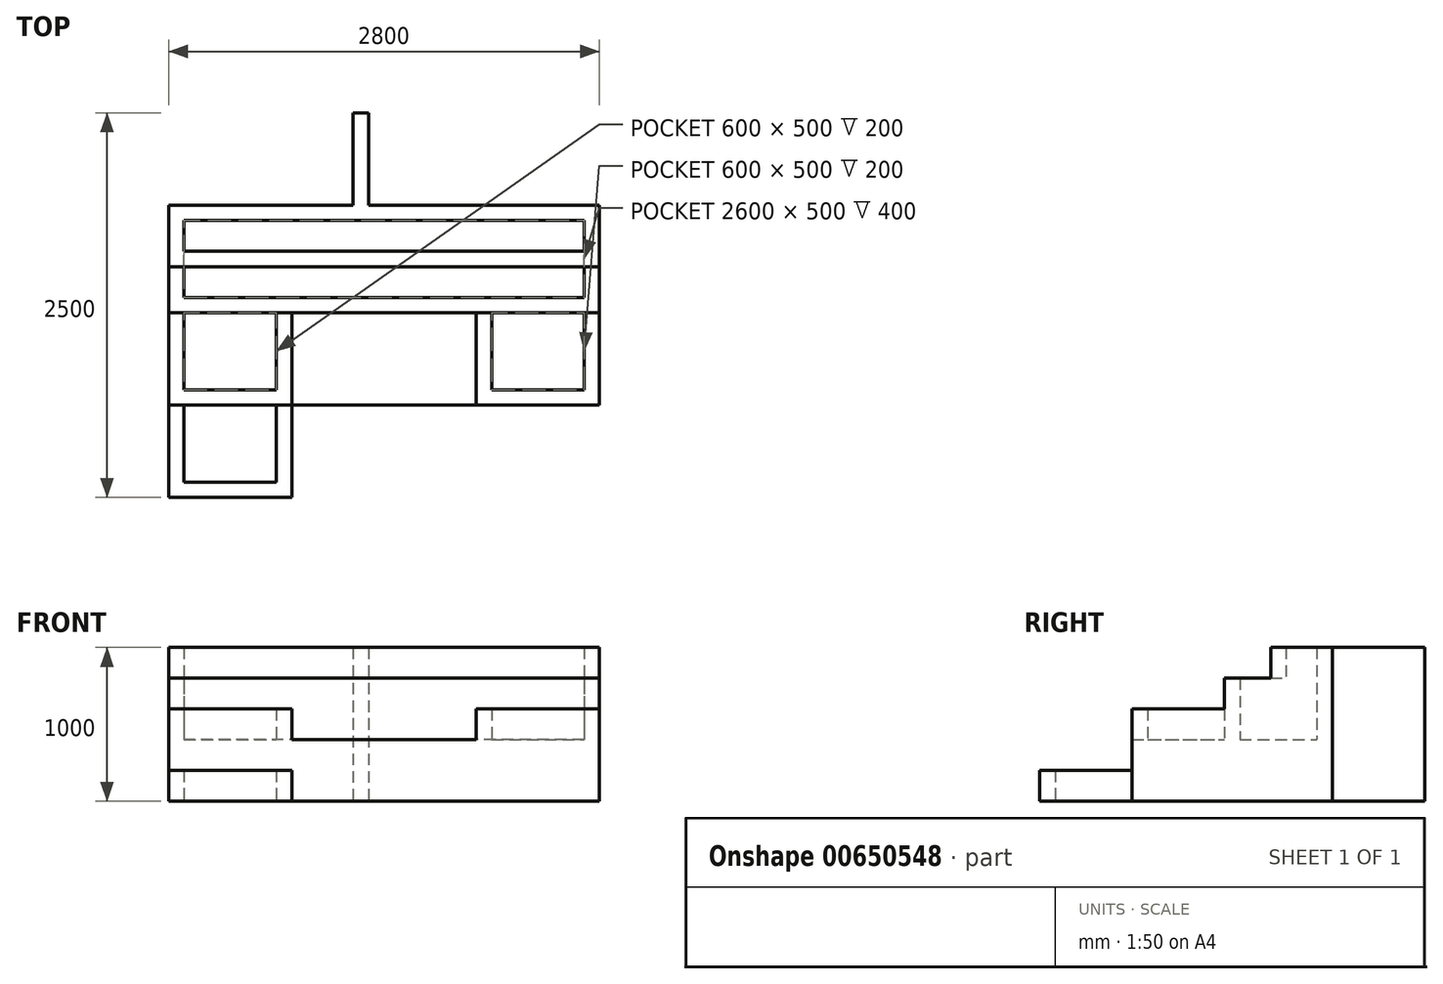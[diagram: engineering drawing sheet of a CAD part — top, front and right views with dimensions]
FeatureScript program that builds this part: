
annotation { "Feature Type Name" : "Feature", "Feature Type Description" : "" }
export const myFeature = defineFeature(function(context is Context, id is Id, definition is map)
    precondition{}
    {
        {
            var Q0;
            Q0=qCreatedBy(makeId("Top.planeOp"),FACE);
            var sketch = newSketch(context, id + "F0", { "sketchPlane" : qUnion([Q0])});
            skLineSegment(sketch, "E0.bottom", {"start": v(0, 0) * mm, "end": v(-2800, 0) * mm});
            skLineSegment(sketch, "E0.top", {"start": v(0, 1300) * mm, "end": v(-2800, 1300) * mm});
            skLineSegment(sketch, "E0.left", {"start": v(0, 0) * mm, "end": v(0, 1300) * mm});
            skLineSegment(sketch, "E0.right", {"start": v(-2800, 0) * mm, "end": v(-2800, 1300) * mm});
            skSolve(sketch);
        }
        {
            var Q0;
            Q0=makeQuery(id+"F0.imprint","IMPRINT",FACE,{"disambiguationData":[TD([[makeQuery(id+"F0.imprint","IMPRINT",EDGE,{"derivedFrom":sQuery(id+"F0.wireOp",EDGE,"E0.bottom")}),-1.0]])]});
            extrude(context, id + "F1", {"entities" : qUnion([Q0]), "depth" : 400 * mm, "offsetDistance" : 25 * mm});
        }
        {
            var Q0;
            Q0=makeQuery(id+"F1.opExtrude","CAP_FACE",FACE,{"disambiguationData":[OSD([sQuery(id+"F0.wireOp",EDGE,"E0.bottom"),sQuery(id+"F0.wireOp",EDGE,"E0.top"),sQuery(id+"F0.wireOp",EDGE,"E0.left"),sQuery(id+"F0.wireOp",EDGE,"E0.right"),sQuery(id+"F0.wireOp",EDGE,"GwEAKkGj-kL16-nnvY-5oqN-CwZshuGkm8Sl.bottom"),sQuery(id+"F0.wireOp",EDGE,"GwEAKkGj-kL16-nnvY-5oqN-CwZshuGkm8Sl.top"),sQuery(id+"F0.wireOp",EDGE,"GwEAKkGj-kL16-nnvY-5oqN-CwZshuGkm8Sl.left"),sQuery(id+"F0.wireOp",EDGE,"GwEAKkGj-kL16-nnvY-5oqN-CwZshuGkm8Sl.right")])],"isStart":false});
            var sketch = newSketch(context, id + "F2", { "sketchPlane" : qUnion([Q0])});
            skLineSegment(sketch, "E1.bottom", {"start": v(0, 600) * mm, "end": v(-2800, 600) * mm});
            skLineSegment(sketch, "E1.top", {"start": v(0, 1300) * mm, "end": v(-2800, 1300) * mm});
            skLineSegment(sketch, "E1.left", {"start": v(0, 600) * mm, "end": v(0, 1300) * mm});
            skLineSegment(sketch, "E1.right", {"start": v(-2800, 600) * mm, "end": v(-2800, 1300) * mm});
            skLineSegment(sketch, "E2.bottom", {"start": v(-100, 700) * mm, "end": v(-2700, 700) * mm});
            skLineSegment(sketch, "E2.top", {"start": v(-100, 1200) * mm, "end": v(-2700, 1200) * mm});
            skLineSegment(sketch, "E2.left", {"start": v(-100, 700) * mm, "end": v(-100, 1200) * mm});
            skLineSegment(sketch, "E2.right", {"start": v(-2700, 700) * mm, "end": v(-2700, 1200) * mm});
            skSolve(sketch);
        }
        {
            var Q0;
            Q0=qSketchRegion(id+"F2",true);
            extrude(context, id + "F3", {"entities" : qUnion([Q0]), "operationType" : NewBodyOperationType.ADD, "depth" : 400 * mm, "offsetDistance" : 25 * mm});
        }
        {
            var Q0;
            Q0=makeQuery(id+"F3.opExtrude","CAP_FACE",FACE,{"disambiguationData":[OSD([sQuery(id+"F2.wireOp",EDGE,"E1.bottom"),sQuery(id+"F2.wireOp",EDGE,"E1.top"),sQuery(id+"F2.wireOp",EDGE,"E1.left"),sQuery(id+"F2.wireOp",EDGE,"E1.right"),sQuery(id+"F2.wireOp",EDGE,"E2.bottom"),sQuery(id+"F2.wireOp",EDGE,"E2.top"),sQuery(id+"F2.wireOp",EDGE,"E2.left"),sQuery(id+"F2.wireOp",EDGE,"E2.right")])],"isStart":false});
            var sketch = newSketch(context, id + "F4", { "sketchPlane" : qUnion([Q0])});
            skLineSegment(sketch, "E3.bottom", {"start": v(0, 900) * mm, "end": v(-2800, 900) * mm});
            skLineSegment(sketch, "E3.top", {"start": v(0, 1300) * mm, "end": v(-2800, 1300) * mm});
            skLineSegment(sketch, "E3.left", {"start": v(0, 900) * mm, "end": v(0, 1300) * mm});
            skLineSegment(sketch, "E3.right", {"start": v(-2800, 900) * mm, "end": v(-2800, 1300) * mm});
            skLineSegment(sketch, "E4.bottom", {"start": v(-100, 1000) * mm, "end": v(-2700, 1000) * mm});
            skLineSegment(sketch, "E4.top", {"start": v(-100, 1200) * mm, "end": v(-2700, 1200) * mm});
            skLineSegment(sketch, "E4.left", {"start": v(-100, 1000) * mm, "end": v(-100, 1200) * mm});
            skLineSegment(sketch, "E4.right", {"start": v(-2700, 1000) * mm, "end": v(-2700, 1200) * mm});
            skSolve(sketch);
        }
        {
            var Q0;
            Q0=qSketchRegion(id+"F4",true);
            extrude(context, id + "F5", {"entities" : qUnion([Q0]), "operationType" : NewBodyOperationType.ADD, "depth" : 200 * mm, "offsetDistance" : 25 * mm});
        }
        {
            var Q0;
            Q0=qCreatedBy(makeId("Top.planeOp"),FACE);
            var sketch = newSketch(context, id + "F6", { "sketchPlane" : qUnion([Q0])});
            skLineSegment(sketch, "E5.bottom", {"start": v(-1500, 1300) * mm, "end": v(-1600, 1300) * mm});
            skLineSegment(sketch, "E5.top", {"start": v(-1500, 1900) * mm, "end": v(-1600, 1900) * mm});
            skLineSegment(sketch, "E5.left", {"start": v(-1500, 1300) * mm, "end": v(-1500, 1900) * mm});
            skLineSegment(sketch, "E5.right", {"start": v(-1600, 1300) * mm, "end": v(-1600, 1900) * mm});
            skSolve(sketch);
        }
        {
            var Q0;
            Q0=qSketchRegion(id+"F6",true);
            extrude(context, id + "F7", {"entities" : qUnion([Q0]), "operationType" : NewBodyOperationType.ADD, "depth" : 1000 * mm, "offsetDistance" : 25 * mm});
        }
        {
            var Q0;
            Q0=makeQuery(id+"F1.opExtrude","CAP_FACE",FACE,{"disambiguationData":[OSD([sQuery(id+"F0.wireOp",EDGE,"E0.bottom"),sQuery(id+"F0.wireOp",EDGE,"E0.top"),sQuery(id+"F0.wireOp",EDGE,"E0.left"),sQuery(id+"F0.wireOp",EDGE,"E0.right"),sQuery(id+"F0.wireOp",EDGE,"GwEAKkGj-kL16-nnvY-5oqN-CwZshuGkm8Sl.bottom"),sQuery(id+"F0.wireOp",EDGE,"GwEAKkGj-kL16-nnvY-5oqN-CwZshuGkm8Sl.top"),sQuery(id+"F0.wireOp",EDGE,"GwEAKkGj-kL16-nnvY-5oqN-CwZshuGkm8Sl.left"),sQuery(id+"F0.wireOp",EDGE,"GwEAKkGj-kL16-nnvY-5oqN-CwZshuGkm8Sl.right")])],"isStart":false});
            var sketch = newSketch(context, id + "F8", { "sketchPlane" : qUnion([Q0])});
            skLineSegment(sketch, "E6.bottom", {"start": v(-2800, 0) * mm, "end": v(-2000, 0) * mm});
            skLineSegment(sketch, "E6.left", {"start": v(-2800, 0) * mm, "end": v(-2800, 600) * mm});
            skLineSegment(sketch, "E6.right", {"start": v(-2000, 0) * mm, "end": v(-2000, 600) * mm});
            skLineSegment(sketch, "E7.bottom", {"start": v(-2700, 100) * mm, "end": v(-2100, 100) * mm});
            skPoint(sketch, "E8.oppositeSnap0", {"position": v(-1400, 600) * mm});
            skLineSegment(sketch, "E8.top", {"start": v(0, 600) * mm, "end": v(-800, 600) * mm});
            skLineSegment(sketch, "E8.right", {"start": v(-800, 0) * mm, "end": v(-800, 600) * mm});
            skLineSegment(sketch, "E9", {"start": v(-2800, 600) * mm, "end": v(-2000, 600) * mm});
            skLineSegment(sketch, "E10", {"start": v(-2700, 100) * mm, "end": v(-2700, 600) * mm});
            skLineSegment(sketch, "E11", {"start": v(-2700, 600) * mm, "end": v(-2100, 600) * mm});
            skLineSegment(sketch, "E12", {"start": v(-2100, 600) * mm, "end": v(-2100, 100) * mm});
            skLineSegment(sketch, "E13", {"start": v(-800, 600) * mm, "end": v(0, 600) * mm});
            skLineSegment(sketch, "E14", {"start": v(-700, 100) * mm, "end": v(-700, 600) * mm});
            skLineSegment(sketch, "E15", {"start": v(-100, 600) * mm, "end": v(-100, 100) * mm});
            skLineSegment(sketch, "E16", {"start": v(-700, 100) * mm, "end": v(-100, 100) * mm});
            skPoint(sketch, "E17.orphan", {"position": v(-100, 0) * mm});
            skLineSegment(sketch, "E18", {"start": v(0, 600) * mm, "end": v(0, 0) * mm});
            skLineSegment(sketch, "E19", {"start": v(0, 0) * mm, "end": v(-800, 0) * mm});
            skSolve(sketch);
        }
        {
            var Q0;
            {var subQ1=sQuery(id+"F8.wireOp",EDGE,"E8.right");Q0=makeQuery(id+"F8.imprint","IMPRINT",FACE,{"disambiguationData":[TD([[makeQuery(id+"F8.imprint","IMPRINT",EDGE,{"derivedFrom":subQ1}),-1.0]])]});}
            var Q1;
            Q1=makeQuery(id+"F8.imprint","IMPRINT",FACE,{"disambiguationData":[TD([[makeQuery(id+"F8.imprint","IMPRINT",EDGE,{"derivedFrom":sQuery(id+"F8.wireOp",EDGE,"E6.bottom")}),-1.0]])]});
            extrude(context, id + "F9", {"entities" : qUnion([Q0, Q1]), "operationType" : NewBodyOperationType.ADD, "depth" : 200 * mm, "offsetDistance" : 25 * mm});
        }
        {
            var Q0;
            Q0=qCreatedBy(makeId("Top.planeOp"),FACE);
            var sketch = newSketch(context, id + "F10", { "sketchPlane" : qUnion([Q0])});
            skLineSegment(sketch, "E20.bottom", {"start": v(-2800, 0) * mm, "end": v(-2000, 0) * mm});
            skLineSegment(sketch, "E20.top", {"start": v(-2800, -600) * mm, "end": v(-2000, -600) * mm});
            skLineSegment(sketch, "E20.left", {"start": v(-2800, 0) * mm, "end": v(-2800, -600) * mm});
            skLineSegment(sketch, "E20.right", {"start": v(-2000, 0) * mm, "end": v(-2000, -600) * mm});
            skLineSegment(sketch, "E21.bottom", {"start": v(-2700, 0) * mm, "end": v(-2100, 0) * mm});
            skLineSegment(sketch, "E21.top", {"start": v(-2700, -500) * mm, "end": v(-2100, -500) * mm});
            skLineSegment(sketch, "E21.left", {"start": v(-2700, 0) * mm, "end": v(-2700, -500) * mm});
            skLineSegment(sketch, "E21.right", {"start": v(-2100, 0) * mm, "end": v(-2100, -500) * mm});
            skSolve(sketch);
        }
        {
            var Q0;
            Q0=makeQuery(id+"F10.imprint","IMPRINT",FACE,{"disambiguationData":[TD([[makeQuery(id+"F10.imprint","IMPRINT",EDGE,{"derivedFrom":sQuery(id+"F10.wireOp",EDGE,"E20.top")}),1.0]])]});
            extrude(context, id + "F11", {"entities" : qUnion([Q0]), "operationType" : NewBodyOperationType.ADD, "depth" : 200 * mm, "offsetDistance" : 25 * mm});
        }
    });
